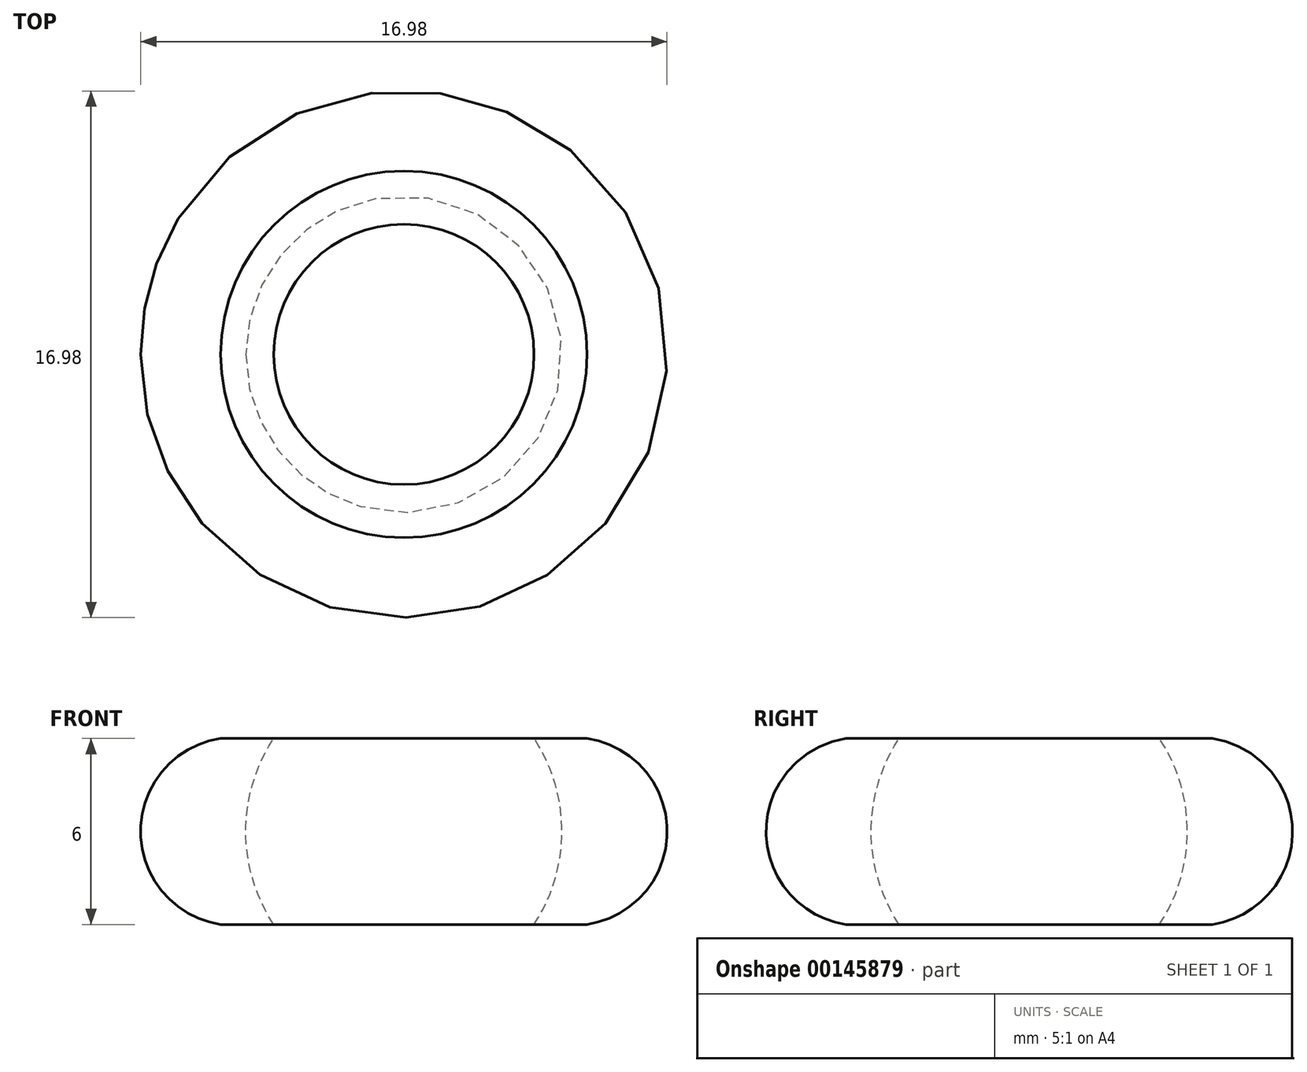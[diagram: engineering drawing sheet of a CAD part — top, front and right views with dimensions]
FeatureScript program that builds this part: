
annotation { "Feature Type Name" : "Feature", "Feature Type Description" : "" }
export const myFeature = defineFeature(function(context is Context, id is Id, definition is map)
    precondition{}
    {
        {
            var Q0;
            Q0=qCreatedBy(makeId("Front.planeOp"),FACE);
            var sketch = newSketch(context, id + "F0", { "sketchPlane" : qUnion([Q0])});
            skLineSegment(sketch, "E0", {"start": v(0.02, -117.65) * mm, "end": v(0.02, -111.65) * mm});
            skLineSegment(sketch, "E1", {"start": v(0, 0) * mm, "end": v(0, 10.46) * mm});
            skLineSegment(sketch, "E2", {"start": v(-8.5, 9.97) * mm, "end": v(-8.5, -2.27) * mm, "construction": true});
            skArc(sketch, "E3", {"start": v(-5.91, 6) * mm, "mid": v(-8.5, 3) * mm, "end": v(-5.91, 0) * mm});
            skPoint(sketch, "E4", {"position": v(0, 3) * mm});
            skLineSegment(sketch, "E5", {"start": v(-5.1, 3) * mm, "end": v(-5.1, 9.48) * mm, "construction": true});
            skLineSegment(sketch, "E6", {"start": v(-5.1, 3) * mm, "end": v(-5.1, -2.98) * mm, "construction": true});
            skLineSegment(sketch, "E7", {"start": v(-4.2, 8.47) * mm, "end": v(-4.2, 7.3) * mm, "construction": true});
            skLineSegment(sketch, "E8", {"start": v(-4.2, 7.3) * mm, "end": v(-4.2, -1.2) * mm, "construction": true});
            skArc(sketch, "E9", {"start": v(-4.2, 6) * mm, "mid": v(-5.1, 3) * mm, "end": v(-4.2, 0) * mm});
            skLineSegment(sketch, "E10", {"start": v(-5.91, 6) * mm, "end": v(-4.2, 6) * mm});
            skLineSegment(sketch, "E11", {"start": v(-5.91, 0) * mm, "end": v(-4.2, 0) * mm});
            skSolve(sketch);
        }
        {
            var Q0;
            Q0 = qSketchRegion(id + "F0", true);
            var Q1;
            Q1=sQuery(id+"F0.wireOp",EDGE,"E1");
            revolve(context, id + "F1", {"entities" : qUnion([Q0]), "axis" : qUnion([Q1]), "revolveType" : RevolveType.FULL});
        }
    });
